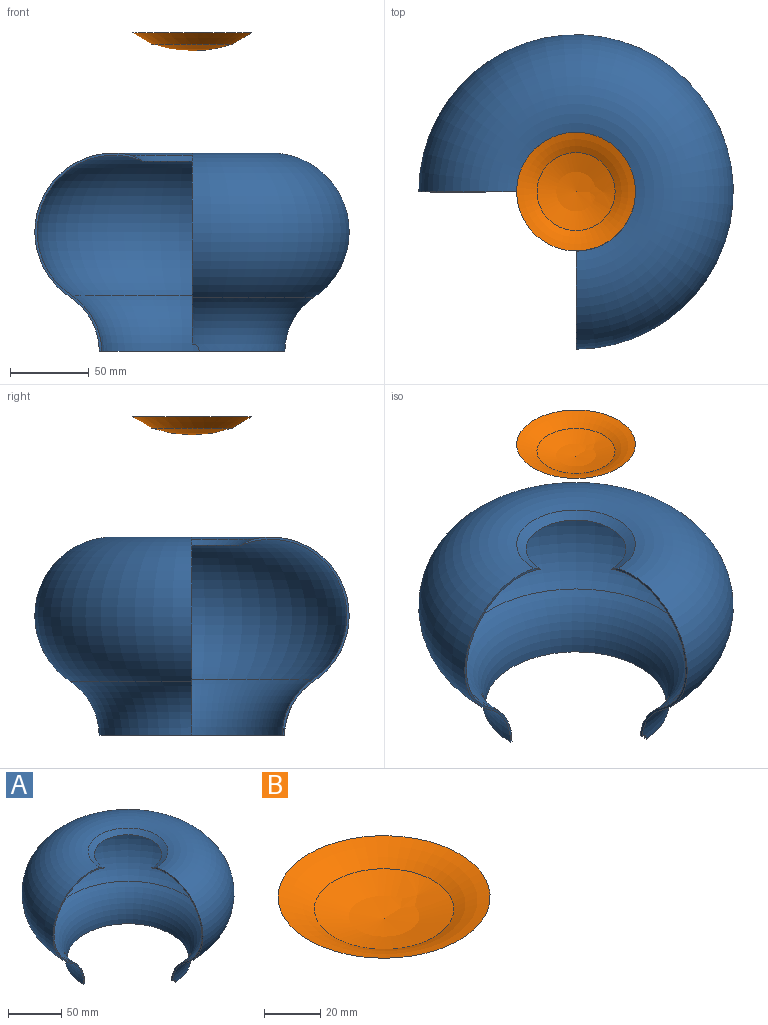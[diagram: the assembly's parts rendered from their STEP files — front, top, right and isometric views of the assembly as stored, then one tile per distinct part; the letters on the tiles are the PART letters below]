
ASSEMBLY  parts=2 mates=1
PART A: 9 faces, bbox 216.5x216.5x156.2 mm
  f0: torus R=100mm, axis (0,0,-1), area 12468.5mm2, adj f2,f5,f6,f7,f8
  f1: torus R=100mm, axis (0,0,-1), area 12674.8mm2, adj f2,f3,f6,f7,f8
  f2: plane 121.5x68.34mm, normal (-1,0,0), area 267.1mm2, adj f0,f1,f3,f4,f5,f8
  f3: torus R=50mm, axis (0,0,-1), area 53203.8mm2, adj f1,f2,f4,f7
  f4: cone r=31.66mm half-angle=59.6deg, axis (0,0,1), area 1153.6mm2, adj f2,f3,f5,f7
  f5: torus R=50mm, axis (0,0,-1), area 54336.5mm2, adj f0,f2,f4,f7
  f6: plane 118.06x117.88mm, normal (0,0,-1), area 405.2mm2, adj f0,f1,f7,f8
  f7: plane 126x68.34mm, normal (0,-1,0), area 273.8mm2, adj f0,f1,f3,f4,f5,f6
  f8: cylinder r=4.5mm len=4.5mm, axis (0,1,0), area 10.6mm2, adj f0,f1,f2,f6
PART B: 4 faces, bbox 108.2x108.2x14.5 mm
  f0: sphere r=76mm, area 1992.3mm2, adj f1
  f1: torus R=50mm, axis (0,0,1), area 2739.6mm2, adj f0,f2
  f2: cone r=25.68mm half-angle=59.6deg, axis (0,0,1), area 2789.4mm2, adj f1,f3
  f3: sphere r=78mm, area 2130.4mm2, adj f2
PLACE A t=(-169.93,-2.01,-89.43)mm
PLACE B t=(-179.53,-2.01,92.28)mm
MATE slider A.f0 <-> B.f1  axis (0,0,-1) through (-169.93,-2.01,35.04)mm
